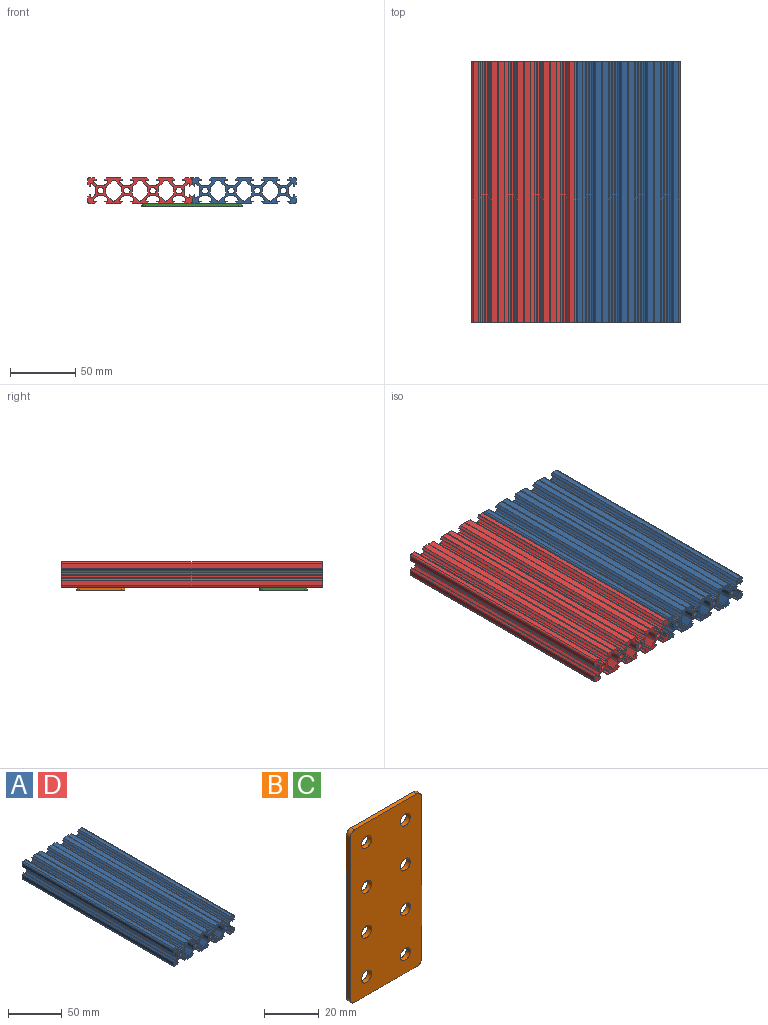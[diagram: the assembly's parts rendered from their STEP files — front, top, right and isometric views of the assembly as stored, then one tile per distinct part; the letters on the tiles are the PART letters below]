
ASSEMBLY  parts=4 mates=3
PART A: 342 faces, bbox 80x200x20 mm
  f0: plane 200x4.28mm, normal (0.71,0,0.71), area 1209.7mm2, adj f1,f333,f340,f341
  f1: cylinder r=2mm len=200mm, axis (0,1,0), area 314.2mm2, adj f0,f2,f340,f341
  f2: plane 200x3.8mm, normal (1,0,0), area 759.5mm2, adj f1,f3,f340,f341
  f3: cylinder r=2mm len=200mm, axis (0,1,0), area 314.2mm2, adj f2,f4,f340,f341
  f4: plane 200x4.28mm, normal (0.71,0,-0.71), area 1209.7mm2, adj f3,f5,f340,f341
  f5: cylinder r=1.4mm len=200mm, axis (0,1,0), area 219.9mm2, adj f4,f6,f340,f341
  f6: plane 200x0.29mm, normal (0,0,-1), area 58.9mm2, adj f5,f7,f340,f341
  f7: cylinder r=1.4mm len=200mm, axis (0,1,0), area 219.9mm2, adj f6,f8,f340,f341
  f8: plane 200x4.28mm, normal (-0.71,0,-0.71), area 1209.7mm2, adj f7,f9,f340,f341
  f9: cylinder r=2mm len=200mm, axis (0,1,0), area 314.2mm2, adj f8,f10,f340,f341
  f10: plane 200x3.8mm, normal (-1,0,0), area 759.5mm2, adj f9,f11,f340,f341
  f11: cylinder r=2mm len=200mm, axis (0,1,0), area 314.2mm2, adj f10,f12,f340,f341
  f12: plane 200x4.28mm, normal (-0.71,0,0.71), area 1209.7mm2, adj f11,f13,f340,f341
  f13: cylinder r=1.4mm len=200mm, axis (0,1,0), area 219.9mm2, adj f12,f14,f340,f341
  f14: plane 200x0.29mm, normal (0,0,1), area 58.9mm2, adj f13,f333,f340,f341
  f15: plane 200x0.24mm, normal (0.55,0,-0.83), area 57mm2, adj f16,f336,f340,f341
  f16: plane 200x0.24mm, normal (-0.55,0,-0.83), area 57mm2, adj f15,f17,f340,f341
  f17: cylinder r=0.25mm len=200mm, axis (0,1,0), area 29.4mm2, adj f16,f18,f340,f341
  f18: plane 200x4.79mm, normal (0,0,-1), area 958.9mm2, adj f17,f19,f340,f341
  f19: cylinder r=0.25mm len=200mm, axis (0,1,0), area 39.3mm2, adj f18,f20,f340,f341
  f20: plane 200x1.5mm, normal (0.71,0,-0.71), area 424.3mm2, adj f19,f21,f340,f341
  f21: cylinder r=0.25mm len=200mm, axis (0,1,0), area 117.8mm2, adj f20,f22,f340,f341
  f22: plane 200x1.77mm, normal (0,0,1), area 354mm2, adj f21,f23,f340,f341
  f23: cylinder r=0.2mm len=200mm, axis (0,1,0), area 62.8mm2, adj f22,f24,f340,f341
  f24: plane 200x0.81mm, normal (1,0,0), area 162.6mm2, adj f23,f25,f340,f341
  f25: cylinder r=1mm len=200mm, axis (0,1,0), area 157.1mm2, adj f24,f26,f340,f341
  f26: plane 200x1.69mm, normal (0.71,0,-0.71), area 479.2mm2, adj f25,f27,f340,f341
  f27: cylinder r=2mm len=200mm, axis (0,1,0), area 314.2mm2, adj f26,f28,f340,f341
  f28: plane 200x1.56mm, normal (0,0,-1), area 312.2mm2, adj f27,f29,f340,f341
  f29: cylinder r=0.25mm len=200mm, axis (0,1,0), area 33.7mm2, adj f28,f30,f340,f341
  f30: plane 200x0.18mm, normal (0.62,0,-0.78), area 46.5mm2, adj f29,f31,f340,f341
  f31: plane 200x0.18mm, normal (-0.62,0,-0.78), area 46.5mm2, adj f30,f32,f340,f341
  f32: cylinder r=0.25mm len=200mm, axis (0,1,0), area 33.7mm2, adj f31,f33,f340,f341
  f33: plane 200x1.56mm, normal (0,0,-1), area 312.2mm2, adj f32,f34,f340,f341
  f34: cylinder r=2mm len=200mm, axis (0,1,0), area 314.2mm2, adj f33,f35,f340,f341
  f35: plane 200x1.69mm, normal (-0.71,0,-0.71), area 479.2mm2, adj f34,f36,f340,f341
  f36: cylinder r=1mm len=200mm, axis (0,1,0), area 157.1mm2, adj f35,f37,f340,f341
  f37: plane 200x0.81mm, normal (-1,0,0), area 162.6mm2, adj f36,f38,f340,f341
  f38: cylinder r=0.2mm len=200mm, axis (0,1,0), area 62.8mm2, adj f37,f39,f340,f341
  f39: plane 200x1.77mm, normal (0,0,1), area 354mm2, adj f38,f40,f340,f341
  f40: cylinder r=0.25mm len=200mm, axis (0,1,0), area 117.8mm2, adj f39,f41,f340,f341
  f41: plane 200x1.5mm, normal (-0.71,0,-0.71), area 424.3mm2, adj f40,f42,f340,f341
  f42: cylinder r=0.25mm len=200mm, axis (0,1,0), area 39.3mm2, adj f41,f43,f340,f341
  f43: plane 200x4.79mm, normal (0,0,-1), area 958.9mm2, adj f42,f44,f340,f341
  f44: cylinder r=0.25mm len=200mm, axis (0,1,0), area 29.4mm2, adj f43,f45,f340,f341
  f45: plane 200x0.24mm, normal (0.55,0,-0.83), area 57mm2, adj f44,f46,f340,f341
  f46: plane 200x0.24mm, normal (-0.55,0,-0.83), area 57mm2, adj f45,f47,f340,f341
  f47: cylinder r=0.25mm len=200mm, axis (0,1,0), area 29.4mm2, adj f46,f48,f340,f341
  f48: plane 200x4.79mm, normal (0,0,-1), area 958.9mm2, adj f47,f49,f340,f341
  f49: cylinder r=0.25mm len=200mm, axis (0,1,0), area 39.3mm2, adj f48,f50,f340,f341
  f50: plane 200x1.5mm, normal (0.71,0,-0.71), area 424.3mm2, adj f49,f51,f340,f341
  f51: cylinder r=0.25mm len=200mm, axis (0,1,0), area 117.8mm2, adj f50,f52,f340,f341
  f52: plane 200x1.77mm, normal (0,0,1), area 354mm2, adj f51,f53,f340,f341
  f53: cylinder r=0.2mm len=200mm, axis (0,1,0), area 62.8mm2, adj f52,f54,f340,f341
  f54: plane 200x0.81mm, normal (1,0,0), area 162.6mm2, adj f53,f55,f340,f341
  f55: cylinder r=1mm len=200mm, axis (0,1,0), area 157.1mm2, adj f54,f56,f340,f341
  f56: plane 200x1.69mm, normal (0.71,0,-0.71), area 479.2mm2, adj f55,f57,f340,f341
  f57: cylinder r=2mm len=200mm, axis (0,1,0), area 314.2mm2, adj f56,f58,f340,f341
  f58: plane 200x1.56mm, normal (0,0,-1), area 312.2mm2, adj f57,f59,f340,f341
  f59: cylinder r=0.25mm len=200mm, axis (0,1,0), area 33.7mm2, adj f58,f60,f340,f341
  f60: plane 200x0.18mm, normal (0.62,0,-0.78), area 46.5mm2, adj f59,f61,f340,f341
  f61: plane 200x0.18mm, normal (-0.62,0,-0.78), area 46.5mm2, adj f60,f62,f340,f341
  f62: cylinder r=0.25mm len=200mm, axis (0,1,0), area 33.7mm2, adj f61,f63,f340,f341
  f63: plane 200x1.56mm, normal (0,0,-1), area 312.2mm2, adj f62,f64,f340,f341
  f64: cylinder r=2mm len=200mm, axis (0,1,0), area 314.2mm2, adj f63,f65,f340,f341
  f65: plane 200x1.69mm, normal (-0.71,0,-0.71), area 479.2mm2, adj f64,f66,f340,f341
  f66: cylinder r=1mm len=200mm, axis (0,1,0), area 157.1mm2, adj f65,f67,f340,f341
  f67: plane 200x0.81mm, normal (-1,0,0), area 162.6mm2, adj f66,f68,f340,f341
  f68: cylinder r=0.2mm len=200mm, axis (0,1,0), area 62.8mm2, adj f67,f69,f340,f341
  f69: plane 200x1.77mm, normal (0,0,1), area 354mm2, adj f68,f70,f340,f341
  f70: cylinder r=0.25mm len=200mm, axis (0,1,0), area 117.8mm2, adj f69,f71,f340,f341
  f71: plane 200x1.5mm, normal (-0.71,0,-0.71), area 424.3mm2, adj f70,f72,f340,f341
  f72: cylinder r=0.25mm len=200mm, axis (0,1,0), area 39.3mm2, adj f71,f73,f340,f341
  f73: plane 200x3.67mm, normal (0,0,-1), area 734mm2, adj f72,f74,f340,f341
  f74: cylinder r=1.5mm len=200mm, axis (0,1,0), area 471.2mm2, adj f73,f75,f340,f341
  f75: plane 200x3.67mm, normal (1,0,0), area 734mm2, adj f74,f76,f340,f341
  f76: cylinder r=0.25mm len=200mm, axis (0,1,0), area 39.3mm2, adj f75,f77,f340,f341
  f77: plane 200x1.5mm, normal (0.71,0,0.71), area 424.3mm2, adj f76,f78,f340,f341
  f78: cylinder r=0.25mm len=200mm, axis (0,1,0), area 117.8mm2, adj f77,f79,f340,f341
  f79: plane 200x1.77mm, normal (-1,0,0), area 354mm2, adj f78,f80,f340,f341
  f80: cylinder r=0.2mm len=200mm, axis (0,1,0), area 62.8mm2, adj f79,f81,f340,f341
  f81: plane 200x0.81mm, normal (0,0,1), area 162.6mm2, adj f80,f82,f340,f341
  f82: cylinder r=1mm len=200mm, axis (0,1,0), area 157.1mm2, adj f81,f83,f340,f341
  f83: plane 200x1.69mm, normal (0.71,0,0.71), area 479.2mm2, adj f82,f84,f340,f341
  f84: cylinder r=2mm len=200mm, axis (0,1,0), area 314.2mm2, adj f83,f85,f340,f341
  f85: plane 200x1.56mm, normal (1,0,0), area 312.2mm2, adj f84,f86,f340,f341
  f86: cylinder r=0.25mm len=200mm, axis (0,1,0), area 33.7mm2, adj f85,f87,f340,f341
  f87: plane 200x0.18mm, normal (0.78,0,0.62), area 46.5mm2, adj f86,f88,f340,f341
  f88: plane 200x0.18mm, normal (0.78,0,-0.62), area 46.5mm2, adj f87,f89,f340,f341
  f89: cylinder r=0.25mm len=200mm, axis (0,1,0), area 33.7mm2, adj f88,f90,f340,f341
  f90: plane 200x1.56mm, normal (1,0,0), area 312.2mm2, adj f89,f91,f340,f341
  f91: cylinder r=2mm len=200mm, axis (0,1,0), area 314.2mm2, adj f90,f92,f340,f341
  f92: plane 200x1.69mm, normal (0.71,0,-0.71), area 479.2mm2, adj f91,f93,f340,f341
  f93: cylinder r=1mm len=200mm, axis (0,1,0), area 157.1mm2, adj f92,f94,f340,f341
  f94: plane 200x0.81mm, normal (0,0,-1), area 162.6mm2, adj f93,f95,f340,f341
  f95: cylinder r=0.2mm len=200mm, axis (0,1,0), area 62.8mm2, adj f94,f96,f340,f341
  f96: plane 200x1.77mm, normal (-1,0,0), area 354mm2, adj f95,f97,f340,f341
  f97: cylinder r=0.25mm len=200mm, axis (0,1,0), area 117.8mm2, adj f96,f98,f340,f341
  f98: plane 200x1.5mm, normal (0.71,0,-0.71), area 424.3mm2, adj f97,f99,f340,f341
  f99: cylinder r=0.25mm len=200mm, axis (0,1,0), area 39.3mm2, adj f98,f100,f340,f341
  f100: plane 200x3.67mm, normal (1,0,0), area 734mm2, adj f99,f101,f340,f341
  f101: cylinder r=1.5mm len=200mm, axis (0,1,0), area 471.2mm2, adj f100,f102,f340,f341
  f102: plane 200x3.67mm, normal (0,0,1), area 734mm2, adj f101,f103,f340,f341
  f103: cylinder r=0.25mm len=200mm, axis (0,1,0), area 39.3mm2, adj f102,f104,f340,f341
  f104: plane 200x1.5mm, normal (-0.71,0,0.71), area 424.3mm2, adj f103,f105,f340,f341
  f105: cylinder r=0.25mm len=200mm, axis (0,1,0), area 117.8mm2, adj f104,f106,f340,f341
  f106: plane 200x1.77mm, normal (0,0,-1), area 354mm2, adj f105,f107,f340,f341
  f107: cylinder r=0.2mm len=200mm, axis (0,1,0), area 62.8mm2, adj f106,f108,f340,f341
  f108: plane 200x0.81mm, normal (-1,0,0), area 162.6mm2, adj f107,f109,f340,f341
  f109: cylinder r=1mm len=200mm, axis (0,1,0), area 157.1mm2, adj f108,f110,f340,f341
  f110: plane 200x1.69mm, normal (-0.71,0,0.71), area 479.2mm2, adj f109,f111,f340,f341
  f111: cylinder r=2mm len=200mm, axis (0,1,0), area 314.2mm2, adj f110,f112,f340,f341
  f112: plane 200x1.56mm, normal (0,0,1), area 312.2mm2, adj f111,f113,f340,f341
  f113: cylinder r=0.25mm len=200mm, axis (0,1,0), area 33.7mm2, adj f112,f114,f340,f341
  f114: plane 200x0.18mm, normal (-0.62,0,0.78), area 46.5mm2, adj f113,f115,f340,f341
  f115: plane 200x0.18mm, normal (0.62,0,0.78), area 46.5mm2, adj f114,f116,f340,f341
  f116: cylinder r=0.25mm len=200mm, axis (0,1,0), area 33.7mm2, adj f115,f117,f340,f341
  f117: plane 200x1.56mm, normal (0,0,1), area 312.2mm2, adj f116,f118,f340,f341
  f118: cylinder r=2mm len=200mm, axis (0,1,0), area 314.2mm2, adj f117,f119,f340,f341
  f119: plane 200x1.69mm, normal (0.71,0,0.71), area 479.2mm2, adj f118,f120,f340,f341
  f120: cylinder r=1mm len=200mm, axis (0,1,0), area 157.1mm2, adj f119,f121,f340,f341
  f121: plane 200x0.81mm, normal (1,0,0), area 162.6mm2, adj f120,f122,f340,f341
  f122: cylinder r=0.2mm len=200mm, axis (0,1,0), area 62.8mm2, adj f121,f123,f340,f341
  f123: plane 200x1.77mm, normal (0,0,-1), area 354mm2, adj f122,f124,f340,f341
  f124: cylinder r=0.25mm len=200mm, axis (0,1,0), area 117.8mm2, adj f123,f125,f340,f341
  f125: plane 200x1.5mm, normal (0.71,0,0.71), area 424.3mm2, adj f124,f126,f340,f341
  f126: cylinder r=0.25mm len=200mm, axis (0,1,0), area 39.3mm2, adj f125,f127,f340,f341
  f127: plane 200x4.79mm, normal (0,0,1), area 958.9mm2, adj f126,f128,f340,f341
  f128: cylinder r=0.25mm len=200mm, axis (0,1,0), area 29.4mm2, adj f127,f129,f340,f341
  f129: plane 200x0.24mm, normal (-0.55,0,0.83), area 57mm2, adj f128,f130,f340,f341
  f130: plane 200x0.24mm, normal (0.55,0,0.83), area 57mm2, adj f129,f131,f340,f341
  f131: cylinder r=0.25mm len=200mm, axis (0,1,0), area 29.4mm2, adj f130,f132,f340,f341
  f132: plane 200x4.79mm, normal (0,0,1), area 958.9mm2, adj f131,f133,f340,f341
  f133: cylinder r=0.25mm len=200mm, axis (0,1,0), area 39.3mm2, adj f132,f134,f340,f341
  f134: plane 200x1.5mm, normal (-0.71,0,0.71), area 424.3mm2, adj f133,f135,f340,f341
  f135: cylinder r=0.25mm len=200mm, axis (0,1,0), area 117.8mm2, adj f134,f136,f340,f341
  f136: plane 200x1.77mm, normal (0,0,-1), area 354mm2, adj f135,f137,f340,f341
  f137: cylinder r=0.2mm len=200mm, axis (0,1,0), area 62.8mm2, adj f136,f138,f340,f341
  f138: plane 200x0.81mm, normal (-1,0,0), area 162.6mm2, adj f137,f139,f340,f341
  f139: cylinder r=1mm len=200mm, axis (0,1,0), area 157.1mm2, adj f138,f140,f340,f341
  f140: plane 200x1.69mm, normal (-0.71,0,0.71), area 479.2mm2, adj f139,f141,f340,f341
  f141: cylinder r=2mm len=200mm, axis (0,1,0), area 314.2mm2, adj f140,f142,f340,f341
  f142: plane 200x1.56mm, normal (0,0,1), area 312.2mm2, adj f141,f143,f340,f341
  f143: cylinder r=0.25mm len=200mm, axis (0,1,0), area 33.7mm2, adj f142,f144,f340,f341
  f144: plane 200x0.18mm, normal (-0.62,0,0.78), area 46.5mm2, adj f143,f145,f340,f341
  f145: plane 200x0.18mm, normal (0.62,0,0.78), area 46.5mm2, adj f144,f146,f340,f341
  f146: cylinder r=0.25mm len=200mm, axis (0,1,0), area 33.7mm2, adj f145,f147,f340,f341
  f147: plane 200x1.56mm, normal (0,0,1), area 312.2mm2, adj f146,f148,f340,f341
  f148: cylinder r=2mm len=200mm, axis (0,1,0), area 314.2mm2, adj f147,f149,f340,f341
  f149: plane 200x1.69mm, normal (0.71,0,0.71), area 479.2mm2, adj f148,f150,f340,f341
  f150: cylinder r=1mm len=200mm, axis (0,1,0), area 157.1mm2, adj f149,f151,f340,f341
  f151: plane 200x0.81mm, normal (1,0,0), area 162.6mm2, adj f150,f152,f340,f341
  f152: cylinder r=0.2mm len=200mm, axis (0,1,0), area 62.8mm2, adj f151,f153,f340,f341
  f153: plane 200x1.77mm, normal (0,0,-1), area 354mm2, adj f152,f154,f340,f341
  f154: cylinder r=0.25mm len=200mm, axis (0,1,0), area 117.8mm2, adj f153,f155,f340,f341
  f155: plane 200x1.5mm, normal (0.71,0,0.71), area 424.3mm2, adj f154,f156,f340,f341
  f156: cylinder r=0.25mm len=200mm, axis (0,1,0), area 39.3mm2, adj f155,f157,f340,f341
  f157: plane 200x4.79mm, normal (0,0,1), area 958.9mm2, adj f156,f158,f340,f341
  f158: cylinder r=0.25mm len=200mm, axis (0,1,0), area 29.4mm2, adj f157,f159,f340,f341
  f159: plane 200x0.24mm, normal (-0.55,0,0.83), area 57mm2, adj f158,f160,f340,f341
  f160: plane 200x0.24mm, normal (0.55,0,0.83), area 57mm2, adj f159,f161,f340,f341
  f161: cylinder r=0.25mm len=200mm, axis (0,1,0), area 29.4mm2, adj f160,f162,f340,f341
  f162: plane 200x4.79mm, normal (0,0,1), area 958.9mm2, adj f161,f163,f340,f341
  f163: cylinder r=0.25mm len=200mm, axis (0,1,0), area 39.3mm2, adj f162,f164,f340,f341
  f164: plane 200x1.5mm, normal (-0.71,0,0.71), area 424.3mm2, adj f163,f165,f340,f341
  f165: cylinder r=0.25mm len=200mm, axis (0,1,0), area 117.8mm2, adj f164,f166,f340,f341
  f166: plane 200x1.77mm, normal (0,0,-1), area 354mm2, adj f165,f167,f340,f341
  f167: cylinder r=0.2mm len=200mm, axis (0,1,0), area 62.8mm2, adj f166,f168,f340,f341
  f168: plane 200x0.81mm, normal (-1,0,0), area 162.6mm2, adj f167,f169,f340,f341
  f169: cylinder r=1mm len=200mm, axis (0,1,0), area 157.1mm2, adj f168,f170,f340,f341
  f170: plane 200x1.69mm, normal (-0.71,0,0.71), area 479.2mm2, adj f169,f171,f340,f341
  f171: cylinder r=2mm len=200mm, axis (0,1,0), area 314.2mm2, adj f170,f172,f340,f341
  f172: plane 200x1.56mm, normal (0,0,1), area 312.2mm2, adj f171,f173,f340,f341
  f173: cylinder r=0.25mm len=200mm, axis (0,1,0), area 33.7mm2, adj f172,f174,f340,f341
  f174: plane 200x0.18mm, normal (-0.62,0,0.78), area 46.5mm2, adj f173,f175,f340,f341
  f175: plane 200x0.18mm, normal (0.62,0,0.78), area 46.5mm2, adj f174,f176,f340,f341
  f176: cylinder r=0.25mm len=200mm, axis (0,1,0), area 33.7mm2, adj f175,f177,f340,f341
  f177: plane 200x1.56mm, normal (0,0,1), area 312.2mm2, adj f176,f178,f340,f341
  f178: cylinder r=2mm len=200mm, axis (0,1,0), area 314.2mm2, adj f177,f179,f340,f341
  f179: plane 200x1.69mm, normal (0.71,0,0.71), area 479.2mm2, adj f178,f180,f340,f341
  f180: cylinder r=1mm len=200mm, axis (0,1,0), area 157.1mm2, adj f179,f181,f340,f341
  f181: plane 200x0.81mm, normal (1,0,0), area 162.6mm2, adj f180,f182,f340,f341
  f182: cylinder r=0.2mm len=200mm, axis (0,1,0), area 62.8mm2, adj f181,f183,f340,f341
  f183: plane 200x1.77mm, normal (0,0,-1), area 354mm2, adj f182,f184,f340,f341
  f184: cylinder r=0.25mm len=200mm, axis (0,1,0), area 117.8mm2, adj f183,f185,f340,f341
  f185: plane 200x1.5mm, normal (0.71,0,0.71), area 424.3mm2, adj f184,f186,f340,f341
  f186: cylinder r=0.25mm len=200mm, axis (0,1,0), area 39.3mm2, adj f185,f187,f340,f341
  f187: plane 200x4.79mm, normal (0,0,1), area 958.9mm2, adj f186,f188,f340,f341
  f188: cylinder r=0.25mm len=200mm, axis (0,1,0), area 29.4mm2, adj f187,f189,f340,f341
  f189: plane 200x0.24mm, normal (-0.55,0,0.83), area 57mm2, adj f188,f190,f340,f341
  f190: plane 200x0.24mm, normal (0.55,0,0.83), area 57mm2, adj f189,f191,f340,f341
  f191: cylinder r=0.25mm len=200mm, axis (0,1,0), area 29.4mm2, adj f190,f192,f340,f341
  f192: plane 200x4.79mm, normal (0,0,1), area 958.9mm2, adj f191,f193,f340,f341
  f193: cylinder r=0.25mm len=200mm, axis (0,1,0), area 39.3mm2, adj f192,f194,f340,f341
  f194: plane 200x1.5mm, normal (-0.71,0,0.71), area 424.3mm2, adj f193,f195,f340,f341
  f195: cylinder r=0.25mm len=200mm, axis (0,1,0), area 117.8mm2, adj f194,f196,f340,f341
  f196: plane 200x1.77mm, normal (0,0,-1), area 354mm2, adj f195,f197,f340,f341
  f197: cylinder r=0.2mm len=200mm, axis (0,1,0), area 62.8mm2, adj f196,f198,f340,f341
  f198: plane 200x0.81mm, normal (-1,0,0), area 162.6mm2, adj f197,f199,f340,f341
  f199: cylinder r=1mm len=200mm, axis (0,1,0), area 157.1mm2, adj f198,f200,f340,f341
  f200: plane 200x1.69mm, normal (-0.71,0,0.71), area 479.2mm2, adj f199,f201,f340,f341
  f201: cylinder r=2mm len=200mm, axis (0,1,0), area 314.2mm2, adj f200,f202,f340,f341
  f202: plane 200x1.56mm, normal (0,0,1), area 312.2mm2, adj f201,f203,f340,f341
  f203: cylinder r=0.25mm len=200mm, axis (0,1,0), area 33.7mm2, adj f202,f204,f340,f341
  f204: plane 200x0.18mm, normal (-0.62,0,0.78), area 46.5mm2, adj f203,f205,f340,f341
  f205: plane 200x0.18mm, normal (0.62,0,0.78), area 46.5mm2, adj f204,f206,f340,f341
  f206: cylinder r=0.25mm len=200mm, axis (0,1,0), area 33.7mm2, adj f205,f207,f340,f341
  f207: plane 200x1.56mm, normal (0,0,1), area 312.2mm2, adj f206,f208,f340,f341
  f208: cylinder r=2mm len=200mm, axis (0,1,0), area 314.2mm2, adj f207,f209,f340,f341
  f209: plane 200x1.69mm, normal (0.71,0,0.71), area 479.2mm2, adj f208,f210,f340,f341
  f210: cylinder r=1mm len=200mm, axis (0,1,0), area 157.1mm2, adj f209,f211,f340,f341
  f211: plane 200x0.81mm, normal (1,0,0), area 162.6mm2, adj f210,f212,f340,f341
  f212: cylinder r=0.2mm len=200mm, axis (0,1,0), area 62.8mm2, adj f211,f213,f340,f341
  f213: plane 200x1.77mm, normal (0,0,-1), area 354mm2, adj f212,f214,f340,f341
  f214: cylinder r=0.25mm len=200mm, axis (0,1,0), area 117.8mm2, adj f213,f215,f340,f341
  f215: plane 200x1.5mm, normal (0.71,0,0.71), area 424.3mm2, adj f214,f216,f340,f341
  f216: cylinder r=0.25mm len=200mm, axis (0,1,0), area 39.3mm2, adj f215,f217,f340,f341
  f217: plane 200x3.67mm, normal (0,0,1), area 734mm2, adj f216,f218,f340,f341
  f218: cylinder r=1.5mm len=200mm, axis (0,1,0), area 471.2mm2, adj f217,f219,f340,f341
  f219: plane 200x3.67mm, normal (-1,0,0), area 734mm2, adj f218,f220,f340,f341
  f220: cylinder r=0.25mm len=200mm, axis (0,1,0), area 39.3mm2, adj f219,f221,f340,f341
  f221: plane 200x1.5mm, normal (-0.71,0,-0.71), area 424.3mm2, adj f220,f222,f340,f341
  f222: cylinder r=0.25mm len=200mm, axis (0,1,0), area 117.8mm2, adj f221,f223,f340,f341
  f223: plane 200x1.77mm, normal (1,0,0), area 354mm2, adj f222,f224,f340,f341
  f224: cylinder r=0.2mm len=200mm, axis (0,1,0), area 62.8mm2, adj f223,f225,f340,f341
  f225: plane 200x0.81mm, normal (0,0,-1), area 162.6mm2, adj f224,f226,f340,f341
  f226: cylinder r=1mm len=200mm, axis (0,1,0), area 157.1mm2, adj f225,f227,f340,f341
  f227: plane 200x1.69mm, normal (-0.71,0,-0.71), area 479.2mm2, adj f226,f228,f340,f341
  f228: cylinder r=2mm len=200mm, axis (0,1,0), area 314.2mm2, adj f227,f229,f340,f341
  f229: plane 200x1.56mm, normal (-1,0,0), area 312.2mm2, adj f228,f230,f340,f341
  f230: cylinder r=0.25mm len=200mm, axis (0,1,0), area 33.7mm2, adj f229,f231,f340,f341
  f231: plane 200x0.18mm, normal (-0.78,0,-0.62), area 46.5mm2, adj f230,f232,f340,f341
  f232: plane 200x0.18mm, normal (-0.78,0,0.62), area 46.5mm2, adj f231,f233,f340,f341
  f233: cylinder r=0.25mm len=200mm, axis (0,1,0), area 33.7mm2, adj f232,f234,f340,f341
  f234: plane 200x1.56mm, normal (-1,0,0), area 312.2mm2, adj f233,f235,f340,f341
  f235: cylinder r=2mm len=200mm, axis (0,1,0), area 314.2mm2, adj f234,f236,f340,f341
  f236: plane 200x1.69mm, normal (-0.71,0,0.71), area 479.2mm2, adj f235,f237,f340,f341
  f237: cylinder r=1mm len=200mm, axis (0,1,0), area 157.1mm2, adj f236,f238,f340,f341
  f238: plane 200x0.81mm, normal (0,0,1), area 162.6mm2, adj f237,f239,f340,f341
  f239: cylinder r=0.2mm len=200mm, axis (0,1,0), area 62.8mm2, adj f238,f240,f340,f341
  f240: plane 200x1.77mm, normal (1,0,0), area 354mm2, adj f239,f241,f340,f341
  f241: cylinder r=0.25mm len=200mm, axis (0,1,0), area 117.8mm2, adj f240,f242,f340,f341
  f242: plane 200x1.5mm, normal (-0.71,0,0.71), area 424.3mm2, adj f241,f243,f340,f341
  f243: cylinder r=0.25mm len=200mm, axis (0,1,0), area 39.3mm2, adj f242,f244,f340,f341
  f244: plane 200x3.67mm, normal (-1,0,0), area 734mm2, adj f243,f245,f340,f341
  f245: cylinder r=1.5mm len=200mm, axis (0,1,0), area 471.2mm2, adj f244,f246,f340,f341
  f246: plane 200x3.67mm, normal (0,0,-1), area 734mm2, adj f245,f247,f340,f341
  f247: cylinder r=0.25mm len=200mm, axis (0,1,0), area 39.3mm2, adj f246,f248,f340,f341
  f248: plane 200x1.5mm, normal (0.71,0,-0.71), area 424.3mm2, adj f247,f249,f340,f341
  f249: cylinder r=0.25mm len=200mm, axis (0,1,0), area 117.8mm2, adj f248,f250,f340,f341
  f250: plane 200x1.77mm, normal (0,0,1), area 354mm2, adj f249,f251,f340,f341
  f251: cylinder r=0.2mm len=200mm, axis (0,1,0), area 62.8mm2, adj f250,f252,f340,f341
  f252: plane 200x0.81mm, normal (1,0,0), area 162.6mm2, adj f251,f253,f340,f341
  f253: cylinder r=1mm len=200mm, axis (0,1,0), area 157.1mm2, adj f252,f254,f340,f341
  f254: plane 200x1.69mm, normal (0.71,0,-0.71), area 479.2mm2, adj f253,f255,f340,f341
  f255: cylinder r=2mm len=200mm, axis (0,1,0), area 314.2mm2, adj f254,f256,f340,f341
  f256: plane 200x1.56mm, normal (0,0,-1), area 312.2mm2, adj f255,f257,f340,f341
  f257: cylinder r=0.25mm len=200mm, axis (0,1,0), area 33.7mm2, adj f256,f258,f340,f341
  f258: plane 200x0.18mm, normal (0.62,0,-0.78), area 46.5mm2, adj f257,f259,f340,f341
  f259: plane 200x0.18mm, normal (-0.62,0,-0.78), area 46.5mm2, adj f258,f260,f340,f341
  f260: cylinder r=0.25mm len=200mm, axis (0,1,0), area 33.7mm2, adj f259,f261,f340,f341
  f261: plane 200x1.56mm, normal (0,0,-1), area 312.2mm2, adj f260,f262,f340,f341
  f262: cylinder r=2mm len=200mm, axis (0,1,0), area 314.2mm2, adj f261,f263,f340,f341
  f263: plane 200x1.69mm, normal (-0.71,0,-0.71), area 479.2mm2, adj f262,f264,f340,f341
  f264: cylinder r=1mm len=200mm, axis (0,1,0), area 157.1mm2, adj f263,f265,f340,f341
  f265: plane 200x0.81mm, normal (-1,0,0), area 162.6mm2, adj f264,f266,f340,f341
  f266: cylinder r=0.2mm len=200mm, axis (0,1,0), area 62.8mm2, adj f265,f267,f340,f341
  f267: plane 200x1.77mm, normal (0,0,1), area 354mm2, adj f266,f268,f340,f341
  f268: cylinder r=0.25mm len=200mm, axis (0,1,0), area 117.8mm2, adj f267,f269,f340,f341
  f269: plane 200x1.5mm, normal (-0.71,0,-0.71), area 424.3mm2, adj f268,f270,f340,f341
  f270: cylinder r=0.25mm len=200mm, axis (0,1,0), area 39.3mm2, adj f269,f271,f340,f341
  f271: plane 200x4.79mm, normal (0,0,-1), area 958.9mm2, adj f270,f272,f340,f341
  f272: cylinder r=0.25mm len=200mm, axis (0,1,0), area 29.4mm2, adj f271,f273,f340,f341
  f273: plane 200x0.24mm, normal (0.55,0,-0.83), area 57mm2, adj f272,f274,f340,f341
  f274: plane 200x0.24mm, normal (-0.55,0,-0.83), area 57mm2, adj f273,f275,f340,f341
  f275: cylinder r=0.25mm len=200mm, axis (0,1,0), area 29.4mm2, adj f274,f276,f340,f341
  f276: plane 200x4.79mm, normal (0,0,-1), area 958.9mm2, adj f275,f277,f340,f341
  f277: cylinder r=0.25mm len=200mm, axis (0,1,0), area 39.3mm2, adj f276,f278,f340,f341
  f278: plane 200x1.5mm, normal (0.71,0,-0.71), area 424.3mm2, adj f277,f279,f340,f341
  f279: cylinder r=0.25mm len=200mm, axis (0,1,0), area 117.8mm2, adj f278,f280,f340,f341
  f280: plane 200x1.77mm, normal (0,0,1), area 354mm2, adj f279,f281,f340,f341
  f281: cylinder r=0.2mm len=200mm, axis (0,1,0), area 62.8mm2, adj f280,f282,f340,f341
  f282: plane 200x0.81mm, normal (1,0,0), area 162.6mm2, adj f281,f283,f340,f341
  f283: cylinder r=1mm len=200mm, axis (0,1,0), area 157.1mm2, adj f282,f284,f340,f341
  f284: plane 200x1.69mm, normal (0.71,0,-0.71), area 479.2mm2, adj f283,f285,f340,f341
  f285: cylinder r=2mm len=200mm, axis (0,1,0), area 314.2mm2, adj f284,f286,f340,f341
  f286: plane 200x1.56mm, normal (0,0,-1), area 312.2mm2, adj f285,f287,f340,f341
  f287: cylinder r=0.25mm len=200mm, axis (0,1,0), area 33.7mm2, adj f286,f288,f340,f341
  f288: plane 200x0.18mm, normal (0.62,0,-0.78), area 46.5mm2, adj f287,f289,f340,f341
  f289: plane 200x0.18mm, normal (-0.62,0,-0.78), area 46.5mm2, adj f288,f290,f340,f341
  f290: cylinder r=0.25mm len=200mm, axis (0,1,0), area 33.7mm2, adj f289,f291,f340,f341
  f291: plane 200x1.56mm, normal (0,0,-1), area 312.2mm2, adj f290,f292,f340,f341
  f292: cylinder r=2mm len=200mm, axis (0,1,0), area 314.2mm2, adj f291,f293,f340,f341
  f293: plane 200x1.69mm, normal (-0.71,0,-0.71), area 479.2mm2, adj f292,f294,f340,f341
  f294: cylinder r=1mm len=200mm, axis (0,1,0), area 157.1mm2, adj f293,f295,f340,f341
  f295: plane 200x0.81mm, normal (-1,0,0), area 162.6mm2, adj f294,f296,f340,f341
  f296: cylinder r=0.2mm len=200mm, axis (0,1,0), area 62.8mm2, adj f295,f297,f340,f341
  f297: plane 200x1.77mm, normal (0,0,1), area 354mm2, adj f296,f298,f340,f341
  f298: cylinder r=0.25mm len=200mm, axis (0,1,0), area 117.8mm2, adj f297,f299,f340,f341
  f299: plane 200x1.5mm, normal (-0.71,0,-0.71), area 424.3mm2, adj f298,f300,f340,f341
  f300: cylinder r=0.25mm len=200mm, axis (0,1,0), area 39.3mm2, adj f299,f301,f340,f341
  f301: plane 200x4.79mm, normal (0,0,-1), area 958.9mm2, adj f300,f336,f340,f341
  f302: plane 200x3.8mm, normal (-1,0,0), area 759.5mm2, adj f303,f337,f340,f341
  f303: cylinder r=2mm len=200mm, axis (0,1,0), area 314.2mm2, adj f302,f304,f340,f341
  f304: plane 200x4.28mm, normal (-0.71,0,0.71), area 1209.7mm2, adj f303,f305,f340,f341
  f305: cylinder r=1.4mm len=200mm, axis (0,1,0), area 219.9mm2, adj f304,f306,f340,f341
  f306: plane 200x0.29mm, normal (0,0,1), area 58.9mm2, adj f305,f307,f340,f341
  f307: cylinder r=1.4mm len=200mm, axis (0,1,0), area 219.9mm2, adj f306,f308,f340,f341
  f308: plane 200x4.28mm, normal (0.71,0,0.71), area 1209.7mm2, adj f307,f309,f340,f341
  f309: cylinder r=2mm len=200mm, axis (0,1,0), area 314.2mm2, adj f308,f310,f340,f341
  f310: plane 200x3.8mm, normal (1,0,0), area 759.5mm2, adj f309,f311,f340,f341
  f311: cylinder r=2mm len=200mm, axis (0,1,0), area 314.2mm2, adj f310,f312,f340,f341
  f312: plane 200x4.28mm, normal (0.71,0,-0.71), area 1209.7mm2, adj f311,f313,f340,f341
  f313: cylinder r=1.4mm len=200mm, axis (0,1,0), area 219.9mm2, adj f312,f314,f340,f341
  f314: plane 200x0.29mm, normal (0,0,-1), area 58.9mm2, adj f313,f315,f340,f341
  f315: cylinder r=1.4mm len=200mm, axis (0,1,0), area 219.9mm2, adj f314,f316,f340,f341
  f316: plane 200x4.28mm, normal (-0.71,0,-0.71), area 1209.7mm2, adj f315,f337,f340,f341
  f317: plane 200x0.29mm, normal (0,0,1), area 58.9mm2, adj f318,f338,f340,f341
  f318: cylinder r=1.4mm len=200mm, axis (0,1,0), area 219.9mm2, adj f317,f319,f340,f341
  f319: plane 200x4.28mm, normal (0.71,0,0.71), area 1209.7mm2, adj f318,f320,f340,f341
  f320: cylinder r=2mm len=200mm, axis (0,1,0), area 314.2mm2, adj f319,f321,f340,f341
  f321: plane 200x3.8mm, normal (1,0,0), area 759.5mm2, adj f320,f322,f340,f341
  f322: cylinder r=2mm len=200mm, axis (0,1,0), area 314.2mm2, adj f321,f323,f340,f341
  f323: plane 200x4.28mm, normal (0.71,0,-0.71), area 1209.7mm2, adj f322,f324,f340,f341
  f324: cylinder r=1.4mm len=200mm, axis (0,1,0), area 219.9mm2, adj f323,f325,f340,f341
  f325: plane 200x0.29mm, normal (0,0,-1), area 58.9mm2, adj f324,f326,f340,f341
  f326: cylinder r=1.4mm len=200mm, axis (0,1,0), area 219.9mm2, adj f325,f327,f340,f341
  f327: plane 200x4.28mm, normal (-0.71,0,-0.71), area 1209.7mm2, adj f326,f328,f340,f341
  f328: cylinder r=2mm len=200mm, axis (0,1,0), area 314.2mm2, adj f327,f329,f340,f341
  f329: plane 200x3.8mm, normal (-1,0,0), area 759.5mm2, adj f328,f330,f340,f341
  f330: cylinder r=2mm len=200mm, axis (0,1,0), area 314.2mm2, adj f329,f331,f340,f341
  f331: plane 200x4.28mm, normal (-0.71,0,0.71), area 1209.7mm2, adj f330,f338,f340,f341
  f332: cylinder r=2.5mm len=200mm, axis (0,1,0), area 3141.6mm2, adj f340,f341
  f333: cylinder r=1.4mm len=200mm, axis (0,1,0), area 219.9mm2, adj f0,f14,f340,f341
  f334: cylinder r=2.5mm len=200mm, axis (0,1,0), area 3141.6mm2, adj f340,f341
  f335: cylinder r=2.5mm len=200mm, axis (0,1,0), area 3141.6mm2, adj f340,f341
  f336: cylinder r=0.25mm len=200mm, axis (0,1,0), area 29.4mm2, adj f15,f301,f340,f341
  f337: cylinder r=2mm len=200mm, axis (0,1,0), area 314.2mm2, adj f302,f316,f340,f341
  f338: cylinder r=1.4mm len=200mm, axis (0,1,0), area 219.9mm2, adj f317,f331,f340,f341
  f339: cylinder r=2.5mm len=200mm, axis (0,1,0), area 3141.6mm2, adj f340,f341
  f340: plane 80x20mm, normal (0,-1,0), area 604.9mm2, adj f0,f1,f2,f3,f4,f5,f6,f7
  f341: plane 80x20mm, normal (0,1,0), area 604.9mm2, adj f0,f1,f2,f3,f4,f5,f6,f7
PART B: 18 faces, bbox 37x2x77 mm
  f0: cylinder r=2.5mm len=2.5mm, axis (0,1,0), area 7.9mm2, adj f1,f15,f16,f17
  f1: plane 32x2mm, normal (0,0,-1), area 64mm2, adj f0,f2,f16,f17
  f2: cylinder r=2.5mm len=2.5mm, axis (0,1,0), area 7.9mm2, adj f1,f3,f16,f17
  f3: plane 72x2mm, normal (1,0,0), area 144mm2, adj f2,f4,f16,f17
  f4: cylinder r=2.5mm len=2.5mm, axis (0,1,0), area 7.9mm2, adj f3,f5,f16,f17
  f5: plane 32x2mm, normal (0,0,1), area 64mm2, adj f4,f6,f16,f17
  f6: cylinder r=2.5mm len=2.5mm, axis (0,1,0), area 7.9mm2, adj f5,f15,f16,f17
  f7: cylinder r=2.6mm len=5.2mm, axis (0,1,0), area 32.7mm2, adj f16,f17
  f8: cylinder r=2.6mm len=5.2mm, axis (0,1,0), area 32.7mm2, adj f16,f17
  f9: cylinder r=2.6mm len=5.2mm, axis (0,1,0), area 32.7mm2, adj f16,f17
  f10: cylinder r=2.6mm len=5.2mm, axis (0,1,0), area 32.7mm2, adj f16,f17
  f11: cylinder r=2.6mm len=5.2mm, axis (0,1,0), area 32.7mm2, adj f16,f17
  f12: cylinder r=2.6mm len=5.2mm, axis (0,1,0), area 32.7mm2, adj f16,f17
  f13: cylinder r=2.6mm len=5.2mm, axis (0,1,0), area 32.7mm2, adj f16,f17
  f14: cylinder r=2.6mm len=5.2mm, axis (0,1,0), area 32.7mm2, adj f16,f17
  f15: plane 72x2mm, normal (-1,0,0), area 144mm2, adj f0,f6,f16,f17
  f16: plane 77x37mm, normal (0,-1,0), area 2673.7mm2, adj f0,f1,f2,f3,f4,f5,f6,f7
  f17: plane 77x37mm, normal (0,1,0), area 2673.7mm2, adj f0,f1,f2,f3,f4,f5,f6,f7
PART C: same geometry as B
PART D: same geometry as A
PLACE A t=(39.59,94.92,-85.4)mm
PLACE B rot(axis=(-0.58,0.58,-0.58),120deg) t=(-42.28,59.4,-62.07)mm
PLACE C rot(axis=(-0.58,-0.58,0.58),120deg) t=(60.31,-69.55,-62.07)mm
PLACE D t=(-40.41,94.92,-85.4)mm
MATE fastened C.f14 <-> D.f43  axis (0,0,1) through (-20.98,-85.08,-60.07)mm
MATE fastened D.f100 <-> A.f219  axis (1,0,0) through (9.02,-105.08,-41.57)mm
MATE fastened B.f9 <-> D.f18  axis (0,0,1) through (-20.99,74.92,-60.07)mm
